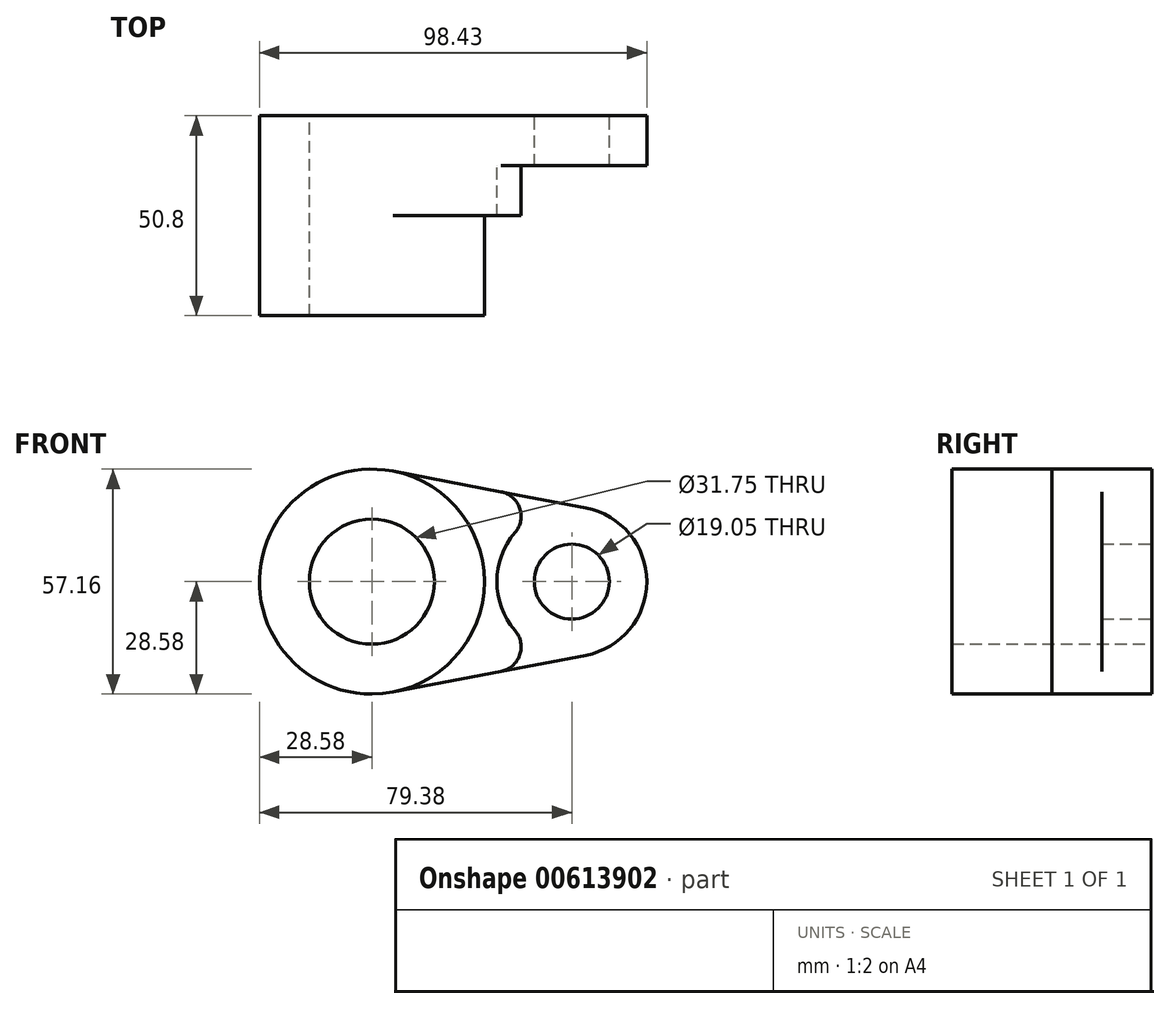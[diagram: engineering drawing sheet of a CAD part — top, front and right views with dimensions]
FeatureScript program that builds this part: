
annotation { "Feature Type Name" : "Feature", "Feature Type Description" : "" }
export const myFeature = defineFeature(function(context is Context, id is Id, definition is map)
    precondition{}
    {
        {
            var Q0;
            Q0=qCreatedBy(makeId("Front.planeOp"),FACE);
            var sketch = newSketch(context, id + "F0", { "sketchPlane" : qUnion([Q0])});
            skCircle(sketch, "E0", {"center": v(0, 0) * mm, "radius": 15.88 * mm});
            skCircle(sketch, "E1", {"center": v(0, 0) * mm, "radius": 28.58 * mm});
            skCircle(sketch, "E2", {"center": v(50.8, 0) * mm, "radius": 19.05 * mm});
            skCircle(sketch, "E3", {"center": v(50.8, 0) * mm, "radius": 9.53 * mm});
            skLineSegment(sketch, "E4", {"start": v(5.36, 28.07) * mm, "end": v(54.37, 18.71) * mm});
            skLineSegment(sketch, "E5", {"start": v(5.36, -28.07) * mm, "end": v(54.37, -18.71) * mm});
            skSolve(sketch);
        }
        {
            var Q0;
            Q0=makeQuery(id+"F0.imprint","IMPRINT",FACE,{"disambiguationData":[TD([[makeQuery(id+"F0.imprint","IMPRINT",EDGE,{"derivedFrom":sQuery(id+"F0.wireOp",EDGE,"E0")}),-1.0]])]});
            var Q1;
            {var subQ0=sQuery(id+"F0.wireOp",EDGE,"E4");Q1=makeQuery(id+"F0.imprint","IMPRINT",FACE,{"disambiguationData":[TD([[makeQuery(id+"F0.imprint","IMPRINT",EDGE,{"derivedFrom":subQ0}),-1.0]])]});}
            extrude(context, id + "F1", {"entities" : qUnion([Q0, Q1]), "depth" : 25.4 * mm, "offsetDistance" : 25.4 * mm});
        }
        {
            var Q0;
            Q0=makeQuery(id+"F0.imprint","IMPRINT",FACE,{"disambiguationData":[TD([[makeQuery(id+"F0.imprint","IMPRINT",EDGE,{"derivedFrom":sQuery(id+"F0.wireOp",EDGE,"E0")}),-1.0]])]});
            extrude(context, id + "F2", {"entities" : qUnion([Q0]), "operationType" : NewBodyOperationType.ADD, "depth" : 50.8 * mm, "offsetDistance" : 25.4 * mm});
        }
        {
            var Q0;
            Q0=makeQuery(id+"F0.imprint","IMPRINT",FACE,{"disambiguationData":[TD([[makeQuery(id+"F0.imprint","IMPRINT",EDGE,{"derivedFrom":sQuery(id+"F0.wireOp",EDGE,"E3")}),-1.0]])]});
            extrude(context, id + "F3", {"entities" : qUnion([Q0]), "operationType" : NewBodyOperationType.ADD, "depth" : 12.7 * mm, "offsetDistance" : 25.4 * mm});
        }
        {
            var Q0;
            {var subQ0=sQuery(id+"F0.wireOp",EDGE,"E2");var subQ1=sQuery(id+"F0.wireOp",EDGE,"E4");Q0=makeQuery(id+"F3.boolean.opBoolean","SPLIT",EDGE,{"disambiguationData":[topologyDisambiguationEdgeConnected([makeQuery(id+"F1.opExtrude","SWEPT_FACE",FACE,{"disambiguationData":[OSD([subQ0])]})])],"derivedFrom":makeQuery(id+"F1.opExtrude","SWEPT_EDGE",EDGE,{"disambiguationData":[OSD([subQ0,subQ1])]})});}
            var Q1;
            {var subQ0=sQuery(id+"F0.wireOp",EDGE,"E2");var subQ1=sQuery(id+"F0.wireOp",EDGE,"E5");Q1=makeQuery(id+"F3.boolean.opBoolean","SPLIT",EDGE,{"disambiguationData":[topologyDisambiguationEdgeConnected([makeQuery(id+"F1.opExtrude","SWEPT_FACE",FACE,{"disambiguationData":[OSD([subQ0])]})])],"derivedFrom":makeQuery(id+"F1.opExtrude","SWEPT_EDGE",EDGE,{"disambiguationData":[OSD([subQ0,subQ1])]})});}
            fillet(context, id + "F4", {"entities" : qUnion([Q0, Q1]), "radius" : 6.35 * mm, "tangentPropagation" : true, "allowEdgeOverflow" : false});
        }
    });
